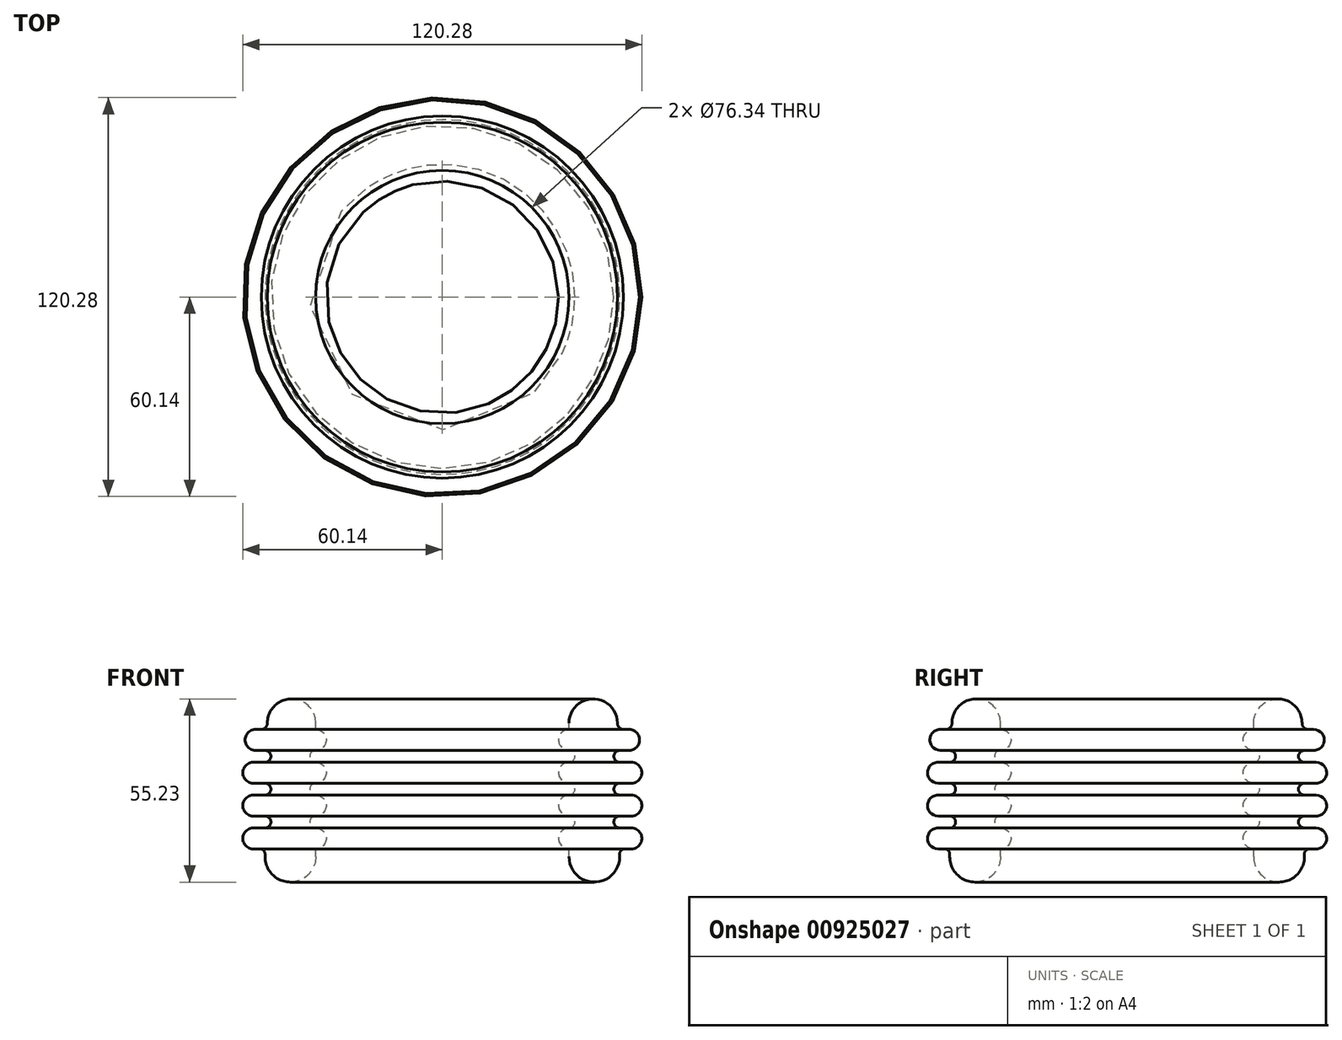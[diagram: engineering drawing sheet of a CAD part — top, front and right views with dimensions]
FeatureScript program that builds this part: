
annotation { "Feature Type Name" : "Feature", "Feature Type Description" : "" }
export const myFeature = defineFeature(function(context is Context, id is Id, definition is map)
    precondition{}
    {
        {
            var Q0;
            Q0=qCreatedBy(makeId("Front.planeOp"),FACE);
            var sketch = newSketch(context, id + "F0", { "sketchPlane" : qUnion([Q0])});
            skLineSegment(sketch, "E0.left", {"start": v(38.17, 20.52) * mm, "end": v(38.17, 18.62) * mm});
            skLineSegment(sketch, "E1", {"start": v(0, 43.04) * mm, "end": v(0, -62.5) * mm, "construction": true});
            skArc(sketch, "E2", {"start": v(52.75, 20.52) * mm, "mid": v(45.46, 27.81) * mm, "end": v(38.17, 20.52) * mm});
            skArc(sketch, "E3", {"start": v(38.17, -19.78) * mm, "mid": v(45.8, -27.42) * mm, "end": v(53.44, -19.78) * mm});
            skLineSegment(sketch, "E4.bottom", {"start": v(54.57, 18.62) * mm, "end": v(56.28, 18.62) * mm});
            skArc(sketch, "E5", {"start": v(52.75, 20.52) * mm, "mid": v(53.28, 19.2) * mm, "end": v(54.57, 18.62) * mm});
            skArc(sketch, "E6", {"start": v(56.28, 12.28) * mm, "mid": v(59.44, 15.45) * mm, "end": v(56.28, 18.62) * mm});
            skPoint(sketch, "E4.left.end.orphan", {"position": v(53.44, 12.28) * mm});
            skPoint(sketch, "E7.orphan", {"position": v(59.78, 12.28) * mm});
            skLineSegment(sketch, "E8", {"start": v(56.28, 12.28) * mm, "end": v(53.44, 12.28) * mm});
            skLineSegment(sketch, "E9.0.1.0", {"start": v(55.27, 8.72) * mm, "end": v(56.97, 8.72) * mm});
            skPoint(sketch, "E9.0.1.1", {"position": v(59.78, 2.38) * mm});
            skArc(sketch, "E9.0.1.3", {"start": v(56.97, 2.38) * mm, "mid": v(60.14, 5.55) * mm, "end": v(56.97, 8.72) * mm});
            skLineSegment(sketch, "E9.0.2.0", {"start": v(55.27, -1.18) * mm, "end": v(56.97, -1.18) * mm});
            skPoint(sketch, "E9.0.2.1", {"position": v(59.78, -7.52) * mm});
            skArc(sketch, "E9.0.2.3", {"start": v(56.97, -7.52) * mm, "mid": v(60.14, -4.35) * mm, "end": v(56.97, -1.18) * mm});
            skLineSegment(sketch, "E9.0.3.0", {"start": v(55.27, -11.08) * mm, "end": v(56.97, -11.08) * mm});
            skPoint(sketch, "E9.0.3.1", {"position": v(59.78, -17.42) * mm});
            skArc(sketch, "E9.0.3.3", {"start": v(56.97, -17.42) * mm, "mid": v(60.14, -14.25) * mm, "end": v(56.97, -11.08) * mm});
            skLineSegment(sketch, "E9.direction1", {"start": v(71.17, 12.28) * mm, "end": v(93.37, 12.28) * mm, "construction": true});
            skLineSegment(sketch, "E10", {"start": v(55.27, 8.72) * mm, "end": v(53.44, 8.72) * mm});
            skArc(sketch, "E11", {"start": v(53.44, 12.28) * mm, "mid": v(51.66, 10.5) * mm, "end": v(53.44, 8.72) * mm});
            skLineSegment(sketch, "E12", {"start": v(56.97, 2.38) * mm, "end": v(53.44, 2.38) * mm});
            skLineSegment(sketch, "E13", {"start": v(55.27, -1.18) * mm, "end": v(53.44, -1.18) * mm});
            skLineSegment(sketch, "E14", {"start": v(56.97, -7.52) * mm, "end": v(53.44, -7.52) * mm});
            skLineSegment(sketch, "E15", {"start": v(55.27, -11.08) * mm, "end": v(53.44, -11.08) * mm});
            skLineSegment(sketch, "E16", {"start": v(56.97, -17.42) * mm, "end": v(54.94, -17.42) * mm});
            skArc(sketch, "E17", {"start": v(53.44, 2.38) * mm, "mid": v(51.66, 0.6) * mm, "end": v(53.44, -1.18) * mm});
            skArc(sketch, "E18", {"start": v(53.44, -7.52) * mm, "mid": v(51.66, -9.3) * mm, "end": v(53.44, -11.08) * mm});
            skLineSegment(sketch, "E19.trimOffspring", {"start": v(53.44, -18.92) * mm, "end": v(53.44, -19.78) * mm});
            skPoint(sketch, "E20.visualSharp", {"position": v(53.44, -17.42) * mm});
            skArc(sketch, "E20.filletArc", {"start": v(54.94, -17.42) * mm, "mid": v(53.88, -17.86) * mm, "end": v(53.44, -18.92) * mm});
            skPoint(sketch, "E21.start.orphan", {"position": v(53.44, 8.42) * mm});
            skArc(sketch, "E22", {"start": v(38.17, -11.08) * mm, "mid": v(35, -14.25) * mm, "end": v(38.17, -17.42) * mm});
            skArc(sketch, "E23.0.1.3", {"start": v(38.17, -1.18) * mm, "mid": v(35, -4.35) * mm, "end": v(38.17, -7.52) * mm});
            skArc(sketch, "E23.0.2.3", {"start": v(38.17, 8.72) * mm, "mid": v(35, 5.55) * mm, "end": v(38.17, 2.38) * mm});
            skArc(sketch, "E23.0.3.3", {"start": v(38.17, 18.62) * mm, "mid": v(35, 15.45) * mm, "end": v(38.17, 12.28) * mm});
            skLineSegment(sketch, "E24.trimOffspring", {"start": v(38.17, -17.42) * mm, "end": v(38.17, -19.78) * mm});
            skArc(sketch, "E25", {"start": v(38.17, -11.08) * mm, "mid": v(39.95, -9.3) * mm, "end": v(38.17, -7.52) * mm});
            skArc(sketch, "E26", {"start": v(38.17, -1.18) * mm, "mid": v(39.95, 0.6) * mm, "end": v(38.17, 2.38) * mm});
            skArc(sketch, "E27", {"start": v(38.17, 8.72) * mm, "mid": v(39.95, 10.5) * mm, "end": v(38.17, 12.28) * mm});
            skSolve(sketch);
        }
        {
            var Q0;
            Q0=makeQuery(id+"F0.imprint","IMPRINT",FACE,{"disambiguationData":[TD([[makeQuery(id+"F0.imprint","IMPRINT",EDGE,{"derivedFrom":sQuery(id+"F0.wireOp",EDGE,"E0.left")}),1.0]])]});
            var Q1;
            Q1=sQuery(id+"F0.wireOp",EDGE,"E2");
            var Q2;
            Q2=sQuery(id+"F0.wireOp",EDGE,"E5");
            var Q3;
            Q3=sQuery(id+"F0.wireOp",EDGE,"E4.bottom");
            var Q4;
            Q4=sQuery(id+"F0.wireOp",EDGE,"E6");
            var Q5;
            Q5=sQuery(id+"F0.wireOp",EDGE,"E4.top");
            var Q6;
            Q6=sQuery(id+"F0.wireOp",EDGE,"E8");
            var Q7;
            Q7=sQuery(id+"F0.wireOp",EDGE,"E10");
            var Q8;
            Q8=sQuery(id+"F0.wireOp",EDGE,"E9.0.1.0");
            var Q9;
            Q9=sQuery(id+"F0.wireOp",EDGE,"E9.0.1.3");
            var Q10;
            Q10=sQuery(id+"F0.wireOp",EDGE,"E9.0.1.2");
            var Q11;
            Q11=sQuery(id+"F0.wireOp",EDGE,"E12");
            var Q12;
            Q12=sQuery(id+"F0.wireOp",EDGE,"E17");
            var Q13;
            Q13=sQuery(id+"F0.wireOp",EDGE,"E11");
            var Q14;
            Q14=sQuery(id+"F0.wireOp",EDGE,"E3");
            var Q15;
            Q15=sQuery(id+"F0.wireOp",EDGE,"E0.left");
            var Q16;
            Q16=sQuery(id+"F0.wireOp",EDGE,"E18");
            var Q17;
            Q17=sQuery(id+"F0.wireOp",EDGE,"E14");
            var Q18;
            Q18=sQuery(id+"F0.wireOp",EDGE,"E9.0.2.2");
            var Q19;
            Q19=sQuery(id+"F0.wireOp",EDGE,"E9.0.2.3");
            var Q20;
            Q20=sQuery(id+"F0.wireOp",EDGE,"E9.0.2.0");
            var Q21;
            Q21=sQuery(id+"F0.wireOp",EDGE,"E15");
            var Q22;
            Q22=sQuery(id+"F0.wireOp",EDGE,"E9.0.3.0");
            var Q23;
            Q23=sQuery(id+"F0.wireOp",EDGE,"E9.0.3.3");
            var Q24;
            Q24=sQuery(id+"F0.wireOp",EDGE,"E9.0.3.2");
            var Q25;
            Q25=sQuery(id+"F0.wireOp",EDGE,"E16");
            var Q26;
            Q26=sQuery(id+"F0.wireOp",EDGE,"E20.filletArc");
            var Q27;
            Q27=sQuery(id+"F0.wireOp",EDGE,"E19.trimOffspring");
            var Q28;
            Q28=sQuery(id+"F0.wireOp",EDGE,"E1");
            revolve(context, id + "F1", {"surfaceOperationType" : NewSurfaceOperationType.NEW, "entities" : qUnion([Q0]), "surfaceEntities" : qUnion([Q1, Q2, Q3, Q4, Q5, Q6, Q7, Q8, Q9, Q10, Q11, Q12, Q13, Q14, Q15, Q16, Q17, Q18, Q19, Q20, Q21, Q22, Q23, Q24, Q25, Q26, Q27]), "axis" : qUnion([Q28]), "revolveType" : RevolveType.FULL});
        }
    });
